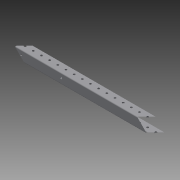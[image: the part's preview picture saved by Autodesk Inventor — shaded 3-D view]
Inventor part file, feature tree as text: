
AUTODESK INVENTOR PART (.ipt)
format: ipt  version: 2015 SP1 (Build 190203100, 203)  size: 157,696 bytes
history: native  units: in
note: dims shown in document units (in); Inventor stores cm internally (conversion verified against a paired STEP export)
features: sketch x5, extrude x3, hole x2, projected_geometry x2, pattern_linear x1
ambient origin geometry x8: Origin, YZ Plane, XZ Plane, XY Plane, X Axis, Y Axis, Z Axis, Center Point
bodies: Solid1 (feature_tree)
feature tree (13):
  extrude  "Extrusion1"  Depth=1.25in
  hole  "Hole1"  [1 undecoded]
  pattern_linear  "Rectangular Pattern1"  Spacing1=16.0in  [1 undecoded]
  hole  "Hole2"  [1 undecoded]
  extrude  "Extrusion3"  Depth=1.0in
  extrude  "Extrusion4"  Depth=1.0in
  sketch  "Sketch1"  dims[d0=1.125in d2=1.25in]
  sketch  "Sketch2"  dims[d3=90.0deg d4=1.125in]
  projected_geometry  "Projected Loop1"
  sketch  "Sketch4"  dims[d5=90.0deg]
  sketch  "Sketch5"  dims[d6=0.125in]
  sketch  "Sketch6"  dims[d7=0.125in d8=16.0in d9=0.0in d10=0.5in d11=0.5in d12=0.25in d13=0.75in d14=0.375in d15=0.25in d16=0.5635in d17=1.0in d18=0.8108in d19=7.874in d21=1.0in d28=0.625in d30=5.5in d31=0.25in d32=0.75in d33=0.375in d34=0.25in d35=0.5635in d36=1.0in d37=0.8108in d38=1.0in d39=0.0in d40=0.25in d41=0.5in d42=0.5in d43=1.0in d44=0.0in d45=0.6875in d46=0.6875in]
  projected_geometry  "Projected Loop3"
note: 3 required parameter values undecoded (feature->parameter linkage not recoverable at this tier; creation-order binding heuristic only, values carry confidence <= 0.55)
